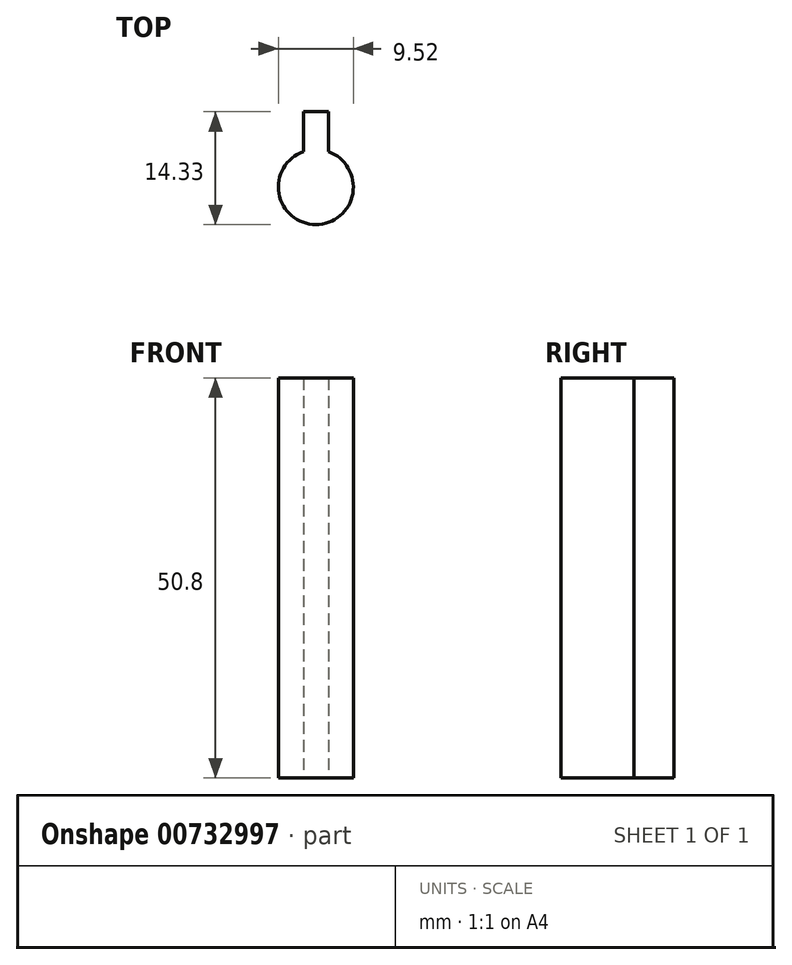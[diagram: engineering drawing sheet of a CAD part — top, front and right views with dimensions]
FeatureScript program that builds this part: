
annotation { "Feature Type Name" : "Feature", "Feature Type Description" : "" }
export const myFeature = defineFeature(function(context is Context, id is Id, definition is map)
    precondition{}
    {
        {
            var Q0;
            Q0=qCreatedBy(makeId("Top.planeOp"),FACE);
            var sketch = newSketch(context, id + "F0", { "sketchPlane" : qUnion([Q0])});
            skCircle(sketch, "E0", {"center": v(0, 0) * mm, "radius": 4.76 * mm});
            skLineSegment(sketch, "E1.bottom", {"start": v(-1.59, 4.5) * mm, "end": v(1.59, 4.5) * mm});
            skLineSegment(sketch, "E1.top", {"start": v(-1.59, 9.57) * mm, "end": v(1.59, 9.57) * mm});
            skLineSegment(sketch, "E1.left", {"start": v(-1.59, 4.5) * mm, "end": v(-1.59, 9.57) * mm});
            skLineSegment(sketch, "E1.right", {"start": v(1.59, 4.5) * mm, "end": v(1.59, 9.57) * mm});
            skSolve(sketch);
        }
        {
            var Q0;
            Q0 = qSketchRegion(id + "F0", true);
            extrude(context, id + "F1", {"entities" : qUnion([Q0]), "depth" : 50.8 * mm, "offsetDistance" : 25.4 * mm});
        }
    });
